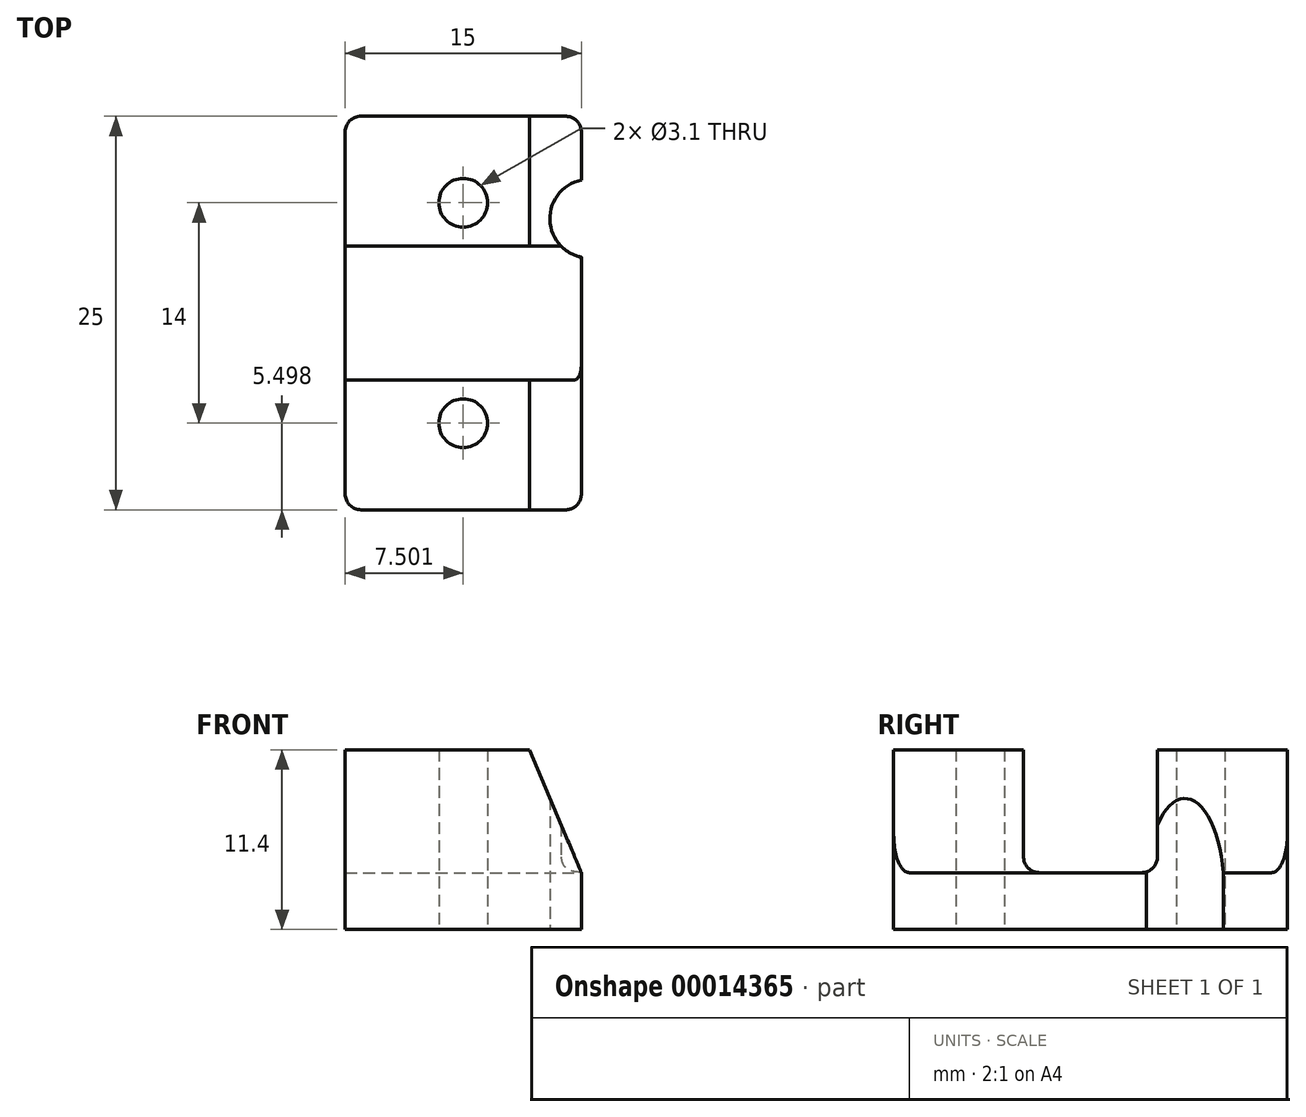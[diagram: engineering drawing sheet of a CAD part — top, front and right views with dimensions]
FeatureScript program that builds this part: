
annotation { "Feature Type Name" : "Feature", "Feature Type Description" : "" }
export const myFeature = defineFeature(function(context is Context, id is Id, definition is map)
    precondition{}
    {
        {
            var Q0;
            Q0=qCreatedBy(makeId("Top.planeOp"),FACE);
            var sketch = newSketch(context, id + "F0", { "sketchPlane" : qUnion([Q0])});
            skLineSegment(sketch, "E0.bottom", {"start": v(-21.78, 14.7) * mm, "end": v(-6.78, 14.7) * mm});
            skLineSegment(sketch, "E0.top", {"start": v(-21.78, -10.3) * mm, "end": v(-6.78, -10.3) * mm});
            skLineSegment(sketch, "E0.left", {"start": v(-21.78, 14.7) * mm, "end": v(-21.78, -10.3) * mm});
            skLineSegment(sketch, "E0.right", {"start": v(-6.78, 14.7) * mm, "end": v(-6.78, -10.3) * mm});
            skCircle(sketch, "E1", {"center": v(-14.28, 9.2) * mm, "radius": 1.55 * mm});
            skCircle(sketch, "E2", {"center": v(-14.28, -4.8) * mm, "radius": 1.55 * mm});
            skLineSegment(sketch, "E3", {"start": v(-21.78, 6.16) * mm, "end": v(-6.78, 6.16) * mm});
            skLineSegment(sketch, "E4", {"start": v(-21.78, -1.74) * mm, "end": v(-6.78, -1.74) * mm});
            skSolve(sketch);
        }
        {
            var Q0;
            Q0=qSketchRegion(id+"F0",true);
            extrude(context, id + "F1", {"entities" : qUnion([Q0]), "depth" : 11.4 * mm});
        }
        {
            var Q0;
            Q0=makeQuery(id+"F1.opExtrude","SWEPT_FACE",FACE,{"disambiguationData":[OSD([sQuery(id+"F0.wireOp",EDGE,"E0.right")])]});
            var sketch = newSketch(context, id + "F2", { "sketchPlane" : qUnion([Q0])});
            skLineSegment(sketch, "E5.bottom", {"start": v(-2.04, 11.4) * mm, "end": v(6.46, 11.4) * mm});
            skLineSegment(sketch, "E5.top", {"start": v(-2.04, 3.6) * mm, "end": v(6.46, 3.6) * mm});
            skLineSegment(sketch, "E5.left", {"start": v(-2.04, 11.4) * mm, "end": v(-2.04, 3.6) * mm});
            skLineSegment(sketch, "E5.right", {"start": v(6.46, 11.4) * mm, "end": v(6.46, 3.6) * mm});
            skSolve(sketch);
        }
        {
            var Q0;
            Q0=makeQuery(id+"F2.imprint","IMPRINT",FACE,{"disambiguationData":[TD([[makeQuery(id+"F2.imprint","IMPRINT",EDGE,{"derivedFrom":sQuery(id+"F2.wireOp",EDGE,"E5.bottom")}),1.0]])]});
            var Q1;
            Q1=makeQuery(id+"F1.opExtrude","SWEPT_FACE",FACE,{"disambiguationData":[OSD([sQuery(id+"F0.wireOp",EDGE,"E0.left")])]});
            extrude(context, id + "F3", {"entities" : qUnion([Q0]), "operationType" : NewBodyOperationType.REMOVE, "endBound" : BoundingType.UP_TO_SURFACE, "oppositeDirection" : true, "endBoundEntityFace" : qUnion([Q1]), "depth" : 25 * mm});
        }
        {
            var Q0;
            Q0=makeQuery(id+"F3.boolean.opBoolean","COPY",EDGE,{"derivedFrom":makeQuery(id+"F3.opExtrude","SWEPT_EDGE",EDGE,{"disambiguationData":[OSD([sQuery(id+"F2.wireOp",EDGE,"E5.top"),sQuery(id+"F2.wireOp",EDGE,"E5.left")])]})});
            var Q1;
            Q1=makeQuery(id+"F3.boolean.opBoolean","COPY",EDGE,{"derivedFrom":makeQuery(id+"F3.opExtrude","SWEPT_EDGE",EDGE,{"disambiguationData":[OSD([sQuery(id+"F2.wireOp",EDGE,"E5.top"),sQuery(id+"F2.wireOp",EDGE,"E5.right")])]})});
            fillet(context, id + "F4", {"entities" : qUnion([Q0, Q1]), "radius" : 1 * mm, "tangentPropagation" : true, "allowEdgeOverflow" : false});
        }
        {
            var Q0;
            Q0=makeQuery(id+"F1.opExtrude","SWEPT_FACE",FACE,{"disambiguationData":[OSD([sQuery(id+"F0.wireOp",EDGE,"E0.top")])]});
            var sketch = newSketch(context, id + "F5", { "sketchPlane" : qUnion([Q0])});
            skLineSegment(sketch, "E6", {"start": v(-10.08, 11.4) * mm, "end": v(-6.78, 3.6) * mm});
            skSolve(sketch);
        }
        {
            var Q0;
            Q0=qSketchRegion(id+"F5",true);
            var Q1;
            {var subQ2=sQuery(id+"F5.wireOp",EDGE,"E6");Q1=makeQuery(id+"F5.imprint","IMPRINT",FACE,{"disambiguationData":[TD([[makeQuery(id+"F5.imprint","IMPRINT",EDGE,{"derivedFrom":subQ2}),1.0]])]});}
            var Q2;
            Q2=makeQuery(id+"F1.opExtrude","SWEPT_FACE",FACE,{"disambiguationData":[OSD([sQuery(id+"F0.wireOp",EDGE,"E0.bottom")])]});
            extrude(context, id + "F6", {"entities" : qUnion([Q0, Q1]), "operationType" : NewBodyOperationType.REMOVE, "endBound" : BoundingType.UP_TO_SURFACE, "oppositeDirection" : true, "endBoundEntityFace" : qUnion([Q2]), "depth" : 25 * mm});
        }
        {
            var Q0;
            Q0=makeQuery(id+"F1.opExtrude","SWEPT_EDGE",EDGE,{"disambiguationData":[OSD([sQuery(id+"F0.wireOp",EDGE,"E0.top"),sQuery(id+"F0.wireOp",EDGE,"E0.right")])]});
            var Q1;
            Q1=makeQuery(id+"F1.opExtrude","SWEPT_EDGE",EDGE,{"disambiguationData":[OSD([sQuery(id+"F0.wireOp",EDGE,"E0.bottom"),sQuery(id+"F0.wireOp",EDGE,"E0.right")])]});
            var Q2;
            Q2=makeQuery(id+"F1.opExtrude","SWEPT_EDGE",EDGE,{"disambiguationData":[OSD([sQuery(id+"F0.wireOp",EDGE,"E0.top"),sQuery(id+"F0.wireOp",EDGE,"E0.left")])]});
            var Q3;
            Q3=makeQuery(id+"F1.opExtrude","SWEPT_EDGE",EDGE,{"disambiguationData":[OSD([sQuery(id+"F0.wireOp",EDGE,"E0.bottom"),sQuery(id+"F0.wireOp",EDGE,"E0.left")])]});
            fillet(context, id + "F7", {"entities" : qUnion([Q0, Q1, Q2, Q3]), "radius" : 1 * mm, "tangentPropagation" : true, "allowEdgeOverflow" : false});
        }
        {
            var Q0;
            {var subQ2=sQuery(id+"F0.wireOp",EDGE,"E0.bottom");Q0=makeQuery(id+"F0.imprint","IMPRINT",FACE,{"disambiguationData":[TD([[makeQuery(id+"F0.imprint","IMPRINT",EDGE,{"derivedFrom":subQ2}),-1.0]])]});}
            var sketch = newSketch(context, id + "F8", { "sketchPlane" : qUnion([Q0])});
            skCircle(sketch, "E7", {"center": v(-6.28, 8.2) * mm, "radius": 2.5 * mm});
            skSolve(sketch);
        }
        {
            var Q0;
            Q0=qSketchRegion(id+"F8",true);
            extrude(context, id + "F9", {"entities" : qUnion([Q0]), "operationType" : NewBodyOperationType.REMOVE, "depth" : 25 * mm});
        }
    });
